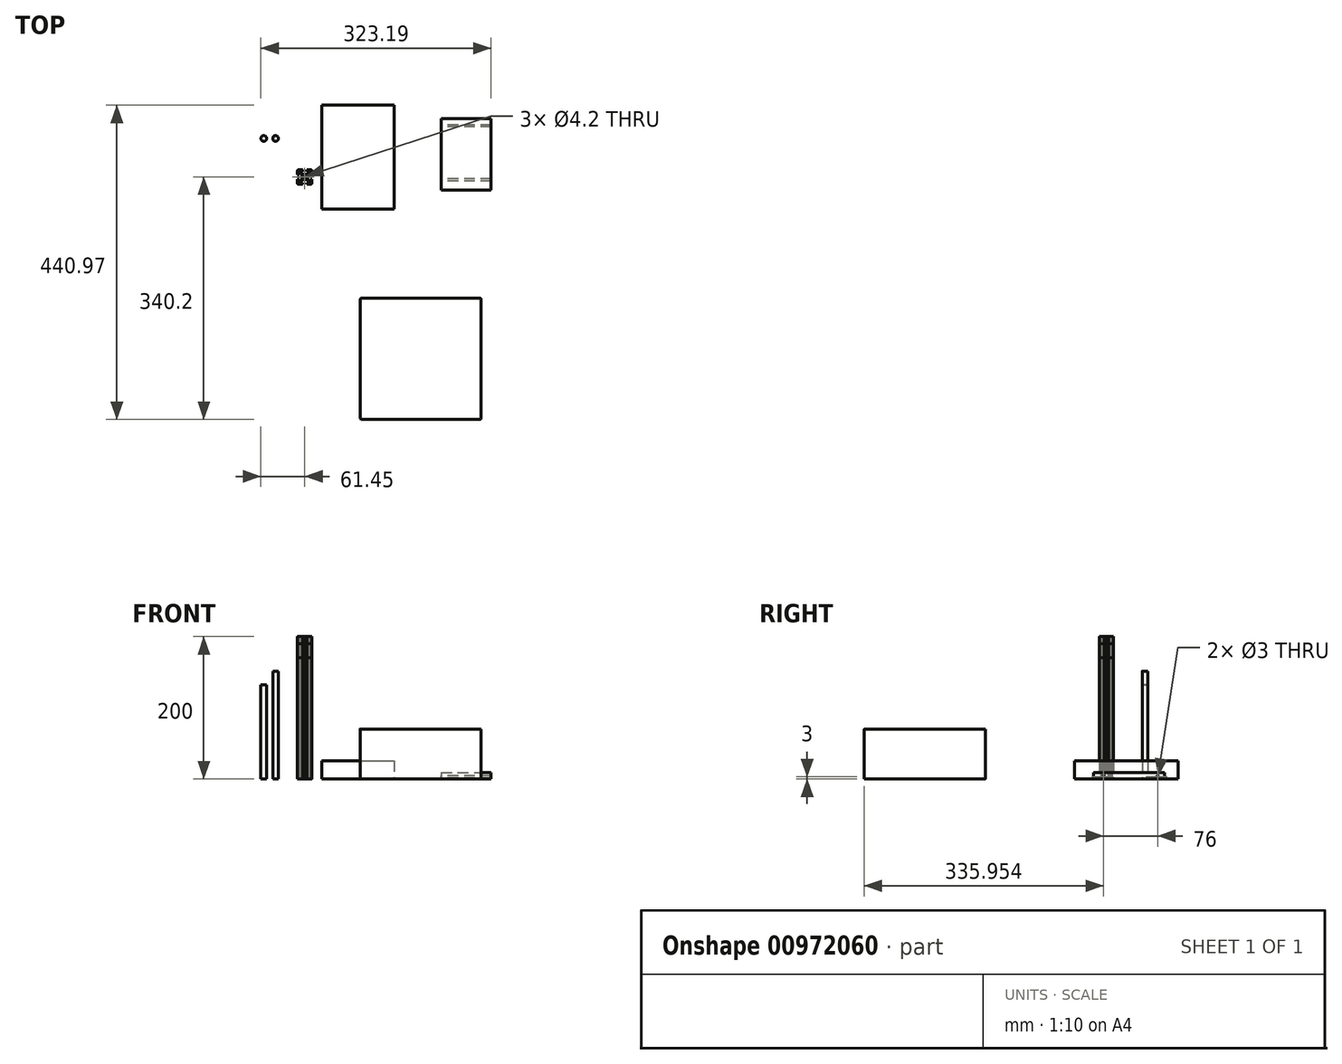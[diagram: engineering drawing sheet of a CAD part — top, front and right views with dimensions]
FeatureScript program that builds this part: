
annotation { "Feature Type Name" : "Feature", "Feature Type Description" : "" }
export const myFeature = defineFeature(function(context is Context, id is Id, definition is map)
    precondition{}
    {
        {
            var Q0;
            Q0=qCreatedBy(makeId("Top.planeOp"),FACE);
            var sketch = newSketch(context, id + "F0", { "sketchPlane" : qUnion([Q0])});
            skCircle(sketch, "E0", {"center": v(-57.45, 54.22) * mm, "radius": 4 * mm});
            skLineSegment(sketch, "E1.bottom", {"start": v(23.74, 100.77) * mm, "end": v(125.34, 100.77) * mm});
            skLineSegment(sketch, "E1.top", {"start": v(23.74, -45.23) * mm, "end": v(125.34, -45.23) * mm});
            skLineSegment(sketch, "E1.left", {"start": v(23.74, 100.77) * mm, "end": v(23.74, -45.23) * mm});
            skLineSegment(sketch, "E1.right", {"start": v(125.34, 100.77) * mm, "end": v(125.34, -45.23) * mm});
            skCircle(sketch, "E2", {"center": v(-40.88, 54.22) * mm, "radius": 4 * mm});
            skLineSegment(sketch, "E3.bottom", {"start": v(191.74, 81.75) * mm, "end": v(261.74, 81.75) * mm});
            skLineSegment(sketch, "E3.top", {"start": v(191.74, -18.25) * mm, "end": v(261.74, -18.25) * mm});
            skLineSegment(sketch, "E3.left", {"start": v(191.74, 81.75) * mm, "end": v(191.74, -18.25) * mm});
            skLineSegment(sketch, "E3.right", {"start": v(261.74, 81.75) * mm, "end": v(261.74, -18.25) * mm});
            skLineSegment(sketch, "E4.bottom", {"start": v(79.85, -170.2) * mm, "end": v(245.85, -170.2) * mm});
            skLineSegment(sketch, "E4.top", {"start": v(79.85, -340.2) * mm, "end": v(245.85, -340.2) * mm});
            skLineSegment(sketch, "E4.left", {"start": v(77.85, -172.2) * mm, "end": v(77.85, -338.2) * mm});
            skLineSegment(sketch, "E4.right", {"start": v(247.85, -172.2) * mm, "end": v(247.85, -338.2) * mm});
            skPoint(sketch, "E5.visualSharp", {"position": v(247.85, -170.2) * mm});
            skArc(sketch, "E5.filletArc", {"start": v(247.85, -172.2) * mm, "mid": v(247.26, -170.79) * mm, "end": v(245.85, -170.2) * mm});
            skPoint(sketch, "E6.visualSharp", {"position": v(247.85, -340.2) * mm});
            skArc(sketch, "E6.filletArc", {"start": v(245.85, -340.2) * mm, "mid": v(247.26, -339.62) * mm, "end": v(247.85, -338.2) * mm});
            skPoint(sketch, "E7.visualSharp", {"position": v(77.85, -340.2) * mm});
            skArc(sketch, "E7.filletArc", {"start": v(77.85, -338.2) * mm, "mid": v(78.43, -339.62) * mm, "end": v(79.85, -340.2) * mm});
            skPoint(sketch, "E8.visualSharp", {"position": v(77.85, -170.2) * mm});
            skArc(sketch, "E8.filletArc", {"start": v(79.85, -170.2) * mm, "mid": v(78.43, -170.79) * mm, "end": v(77.85, -172.2) * mm});
            skLineSegment(sketch, "E9", {"start": v(-8, -3) * mm, "end": v(-10, -3) * mm});
            skLineSegment(sketch, "E10", {"start": v(-10, -3) * mm, "end": v(-10, -9) * mm});
            skArc(sketch, "E11", {"start": v(-10, -9) * mm, "mid": v(-9.7, -9.7) * mm, "end": v(-9, -10) * mm});
            skLineSegment(sketch, "E12", {"start": v(-9, -10) * mm, "end": v(-3, -10) * mm});
            skLineSegment(sketch, "E13", {"start": v(-3, -10) * mm, "end": v(-3, -8) * mm});
            skLineSegment(sketch, "E14", {"start": v(-3, -8) * mm, "end": v(-6, -8) * mm});
            skLineSegment(sketch, "E15", {"start": v(-6, -8) * mm, "end": v(-6, -7.06) * mm});
            skLineSegment(sketch, "E16", {"start": v(-6, -7.06) * mm, "end": v(-2.94, -4) * mm});
            skLineSegment(sketch, "E17", {"start": v(-2.94, -4) * mm, "end": v(-0.52, -4) * mm});
            skLineSegment(sketch, "E18", {"start": v(-0.52, -4) * mm, "end": v(0, -3.7) * mm});
            skLineSegment(sketch, "E19", {"start": v(0, -3.7) * mm, "end": v(0.52, -4) * mm});
            skLineSegment(sketch, "E20", {"start": v(0.52, -4) * mm, "end": v(2.94, -4) * mm});
            skLineSegment(sketch, "E21", {"start": v(2.94, -4) * mm, "end": v(6, -7.06) * mm});
            skLineSegment(sketch, "E22", {"start": v(6, -7.06) * mm, "end": v(6, -8) * mm});
            skLineSegment(sketch, "E23", {"start": v(6, -8) * mm, "end": v(3, -8) * mm});
            skLineSegment(sketch, "E24", {"start": v(3, -8) * mm, "end": v(3, -10) * mm});
            skLineSegment(sketch, "E25", {"start": v(3, -10) * mm, "end": v(9, -10) * mm});
            skArc(sketch, "E26", {"start": v(9, -10) * mm, "mid": v(9.7, -9.7) * mm, "end": v(10, -9) * mm});
            skLineSegment(sketch, "E27", {"start": v(10, -9) * mm, "end": v(10, -3) * mm});
            skLineSegment(sketch, "E28", {"start": v(10, -3) * mm, "end": v(8, -3) * mm});
            skLineSegment(sketch, "E29", {"start": v(8, -3) * mm, "end": v(8, -6) * mm});
            skLineSegment(sketch, "E30", {"start": v(8, -6) * mm, "end": v(7.06, -6) * mm});
            skLineSegment(sketch, "E31", {"start": v(7.06, -6) * mm, "end": v(4, -2.94) * mm});
            skLineSegment(sketch, "E32", {"start": v(4, -2.94) * mm, "end": v(4, -0.52) * mm});
            skLineSegment(sketch, "E33", {"start": v(4, -0.52) * mm, "end": v(3.7, 0) * mm});
            skLineSegment(sketch, "E34", {"start": v(3.7, 0) * mm, "end": v(4, 0.52) * mm});
            skLineSegment(sketch, "E35", {"start": v(4, 0.52) * mm, "end": v(4, 2.94) * mm});
            skLineSegment(sketch, "E36", {"start": v(4, 2.94) * mm, "end": v(7.06, 6) * mm});
            skLineSegment(sketch, "E37", {"start": v(7.06, 6) * mm, "end": v(8, 6) * mm});
            skLineSegment(sketch, "E38", {"start": v(8, 6) * mm, "end": v(8, 3) * mm});
            skLineSegment(sketch, "E39", {"start": v(8, 3) * mm, "end": v(10, 3) * mm});
            skLineSegment(sketch, "E40", {"start": v(10, 3) * mm, "end": v(10, 9) * mm});
            skArc(sketch, "E41", {"start": v(10, 9) * mm, "mid": v(9.7, 9.7) * mm, "end": v(9, 10) * mm});
            skLineSegment(sketch, "E42", {"start": v(9, 10) * mm, "end": v(3, 10) * mm});
            skLineSegment(sketch, "E43", {"start": v(3, 10) * mm, "end": v(3, 8) * mm});
            skLineSegment(sketch, "E44", {"start": v(3, 8) * mm, "end": v(6, 8) * mm});
            skLineSegment(sketch, "E45", {"start": v(6, 8) * mm, "end": v(6, 7.06) * mm});
            skLineSegment(sketch, "E46", {"start": v(6, 7.06) * mm, "end": v(2.94, 4) * mm});
            skLineSegment(sketch, "E47", {"start": v(2.94, 4) * mm, "end": v(0.52, 4) * mm});
            skLineSegment(sketch, "E48", {"start": v(0.52, 4) * mm, "end": v(0, 3.7) * mm});
            skLineSegment(sketch, "E49", {"start": v(0, 3.7) * mm, "end": v(-0.52, 4) * mm});
            skLineSegment(sketch, "E50", {"start": v(-0.52, 4) * mm, "end": v(-2.94, 4) * mm});
            skLineSegment(sketch, "E51", {"start": v(-2.94, 4) * mm, "end": v(-6, 7.06) * mm});
            skLineSegment(sketch, "E52", {"start": v(-6, 7.06) * mm, "end": v(-6, 8) * mm});
            skLineSegment(sketch, "E53", {"start": v(-6, 8) * mm, "end": v(-3, 8) * mm});
            skLineSegment(sketch, "E54", {"start": v(-3, 8) * mm, "end": v(-3, 10) * mm});
            skLineSegment(sketch, "E55", {"start": v(-3, 10) * mm, "end": v(-9, 10) * mm});
            skArc(sketch, "E56", {"start": v(-9, 10) * mm, "mid": v(-9.7, 9.7) * mm, "end": v(-10, 9) * mm});
            skLineSegment(sketch, "E57", {"start": v(-10, 9) * mm, "end": v(-10, 3) * mm});
            skLineSegment(sketch, "E58", {"start": v(-10, 3) * mm, "end": v(-8, 3) * mm});
            skLineSegment(sketch, "E59", {"start": v(-8, 3) * mm, "end": v(-8, 6) * mm});
            skLineSegment(sketch, "E60", {"start": v(-8, 6) * mm, "end": v(-7.06, 6) * mm});
            skLineSegment(sketch, "E61", {"start": v(-7.06, 6) * mm, "end": v(-4, 2.94) * mm});
            skLineSegment(sketch, "E62", {"start": v(-4, 2.94) * mm, "end": v(-4, 0.52) * mm});
            skLineSegment(sketch, "E63", {"start": v(-4, 0.52) * mm, "end": v(-3.7, 0) * mm});
            skLineSegment(sketch, "E64", {"start": v(-3.7, 0) * mm, "end": v(-4, -0.52) * mm});
            skLineSegment(sketch, "E65", {"start": v(-4, -0.52) * mm, "end": v(-4, -2.94) * mm});
            skLineSegment(sketch, "E66", {"start": v(-4, -2.94) * mm, "end": v(-7.06, -6) * mm});
            skLineSegment(sketch, "E67", {"start": v(-7.06, -6) * mm, "end": v(-8, -6) * mm});
            skLineSegment(sketch, "E68", {"start": v(-8, -6) * mm, "end": v(-8, -3) * mm});
            skCircle(sketch, "E69", {"center": v(0, 0) * mm, "radius": 2.1 * mm});
            skSolve(sketch);
        }
        {
            var Q0;
            Q0=makeQuery(id+"F0.imprint","IMPRINT",FACE,{"disambiguationData":[TD([[makeQuery(id+"F0.imprint","IMPRINT",EDGE,{"derivedFrom":sQuery(id+"F0.wireOp",EDGE,"E0")}),1.0]])]});
            extrude(context, id + "F1", {"entities" : qUnion([Q0]), "depth" : 132 * mm, "offsetDistance" : 25 * mm});
        }
        {
            var Q0;
            Q0=makeQuery(id+"F0.imprint","IMPRINT",FACE,{"disambiguationData":[TD([[makeQuery(id+"F0.imprint","IMPRINT",EDGE,{"derivedFrom":sQuery(id+"F0.wireOp",EDGE,"E1.bottom")}),-1.0]])]});
            extrude(context, id + "F2", {"entities" : qUnion([Q0]), "depth" : 25.4 * mm, "offsetDistance" : 25 * mm});
        }
        {
            var Q0;
            Q0=makeQuery(id+"F0.imprint","IMPRINT",FACE,{"disambiguationData":[TD([[makeQuery(id+"F0.imprint","IMPRINT",EDGE,{"derivedFrom":sQuery(id+"F0.wireOp",EDGE,"E2")}),1.0]])]});
            extrude(context, id + "F3", {"entities" : qUnion([Q0]), "depth" : 151.5 * mm, "offsetDistance" : 25 * mm});
        }
        {
            var Q0;
            Q0=makeQuery(id+"F0.imprint","IMPRINT",FACE,{"disambiguationData":[TD([[makeQuery(id+"F0.imprint","IMPRINT",EDGE,{"derivedFrom":sQuery(id+"F0.wireOp",EDGE,"E3.bottom")}),-1.0]])]});
            extrude(context, id + "F4", {"entities" : qUnion([Q0]), "depth" : 9 * mm, "offsetDistance" : 25 * mm});
        }
        {
            var Q0;
            Q0=makeQuery(id+"F4.opExtrude","SWEPT_FACE",FACE,{"disambiguationData":[OSD([sQuery(id+"F0.wireOp",EDGE,"E3.right")])]});
            var sketch = newSketch(context, id + "F5", { "sketchPlane" : qUnion([Q0])});
            skCircle(sketch, "E70", {"center": v(-4.25, 3) * mm, "radius": 1.5 * mm});
            skCircle(sketch, "E71.1.0.0", {"center": v(71.75, 3) * mm, "radius": 1.5 * mm});
            skLineSegment(sketch, "E71.direction1", {"start": v(-4.25, 3) * mm, "end": v(71.75, 3) * mm, "construction": true});
            skSolve(sketch);
        }
        {
            var Q0;
            Q0=sQuery(id+"F5.wireOp",VERTEX,"E70.center");
            var Q1;
            Q1=sQuery(id+"F5.wireOp",VERTEX,"E71.direction1.end");
            var Q2;
            Q2=makeQuery(id+"F4.opExtrude","SWEPT_BODY",BODY,{"disambiguationData":[OSD([sQuery(id+"F0.wireOp",EDGE,"E3.bottom"),sQuery(id+"F0.wireOp",EDGE,"E3.top"),sQuery(id+"F0.wireOp",EDGE,"E3.left"),sQuery(id+"F0.wireOp",EDGE,"E3.right")])]});
            hole(context, id + "F6", {"style" : HoleStyle.SIMPLE, "endStyle" : HoleEndStyle.THROUGH, "holeDiameter" : 3 * mm, "majorDiameter" : 5 * mm, "isTappedThrough" : true, "tappedDepth" : 12 * mm, "tapClearance" : 3, "locations" : qUnion([Q0, Q1]), "scope" : qUnion([Q2]), "startStyle" : HoleStartStyle.PART});
        }
        {
            var Q0;
            Q0=makeQuery(id+"F0.imprint","IMPRINT",FACE,{"disambiguationData":[TD([[makeQuery(id+"F0.imprint","IMPRINT",EDGE,{"derivedFrom":sQuery(id+"F0.wireOp",EDGE,"E4.bottom")}),-1.0]])]});
            extrude(context, id + "F7", {"entities" : qUnion([Q0]), "depth" : 70 * mm, "offsetDistance" : 25 * mm});
        }
        {
            var Q0;
            Q0=makeQuery(id+"F0.imprint","IMPRINT",FACE,{"disambiguationData":[TD([[makeQuery(id+"F0.imprint","IMPRINT",EDGE,{"derivedFrom":sQuery(id+"F0.wireOp",EDGE,"E9")}),1.0]])]});
            extrude(context, id + "F8", {"entities" : qUnion([Q0]), "depth" : 200 * mm, "offsetDistance" : 25 * mm});
        }
        {
            var Q0;
            Q0=makeQuery(id+"F0.imprint","IMPRINT",FACE,{"disambiguationData":[TD([[makeQuery(id+"F0.imprint","IMPRINT",EDGE,{"derivedFrom":sQuery(id+"F0.wireOp",EDGE,"E9")}),1.0]])]});
            extrude(context, id + "F9", {"entities" : qUnion([Q0]), "depth" : 190 * mm, "offsetDistance" : 25 * mm});
        }
        {
            var Q0;
            Q0=makeQuery(id+"F0.imprint","IMPRINT",FACE,{"disambiguationData":[TD([[makeQuery(id+"F0.imprint","IMPRINT",EDGE,{"derivedFrom":sQuery(id+"F0.wireOp",EDGE,"E9")}),1.0]])]});
            extrude(context, id + "F10", {"entities" : qUnion([Q0]), "depth" : 170 * mm, "offsetDistance" : 25 * mm});
        }
    });
